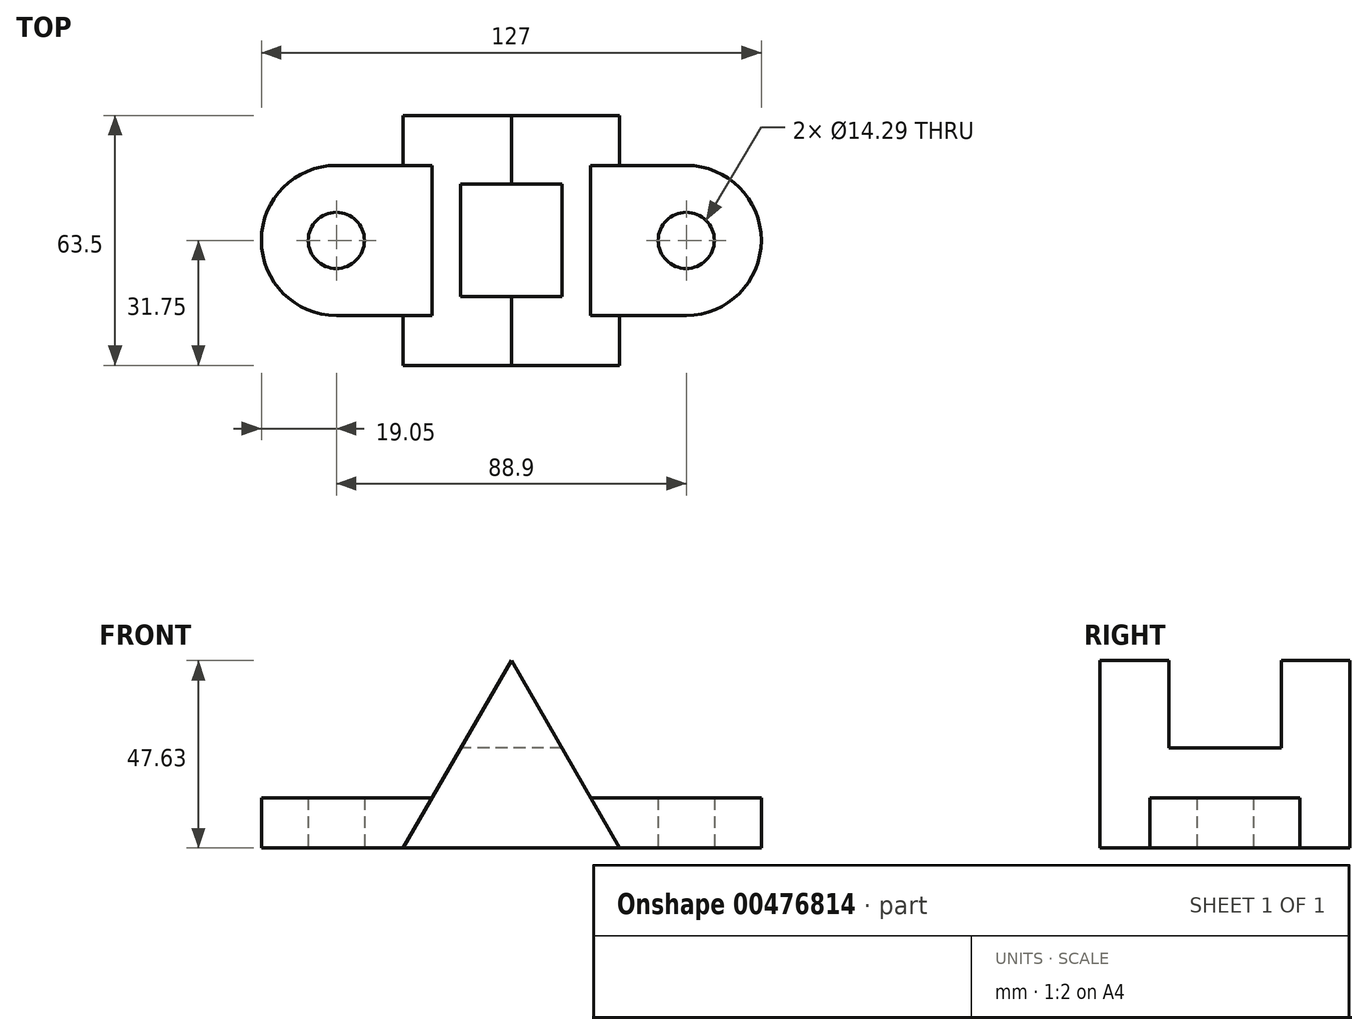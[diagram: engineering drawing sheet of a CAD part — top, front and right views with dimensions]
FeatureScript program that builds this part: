
annotation { "Feature Type Name" : "Feature", "Feature Type Description" : "" }
export const myFeature = defineFeature(function(context is Context, id is Id, definition is map)
    precondition{}
    {
        {
            var Q0;
            Q0=qCreatedBy(makeId("Top.planeOp"),FACE);
            var sketch = newSketch(context, id + "F0", { "sketchPlane" : qUnion([Q0])});
            skArc(sketch, "E0", {"start": v(88.9, -19.05) * mm, "mid": v(107.95, 0) * mm, "end": v(88.9, 19.05) * mm});
            skArc(sketch, "E1", {"start": v(0, 19.05) * mm, "mid": v(-19.05, 0) * mm, "end": v(0, -19.05) * mm});
            skLineSegment(sketch, "E2", {"start": v(0, 19.05) * mm, "end": v(88.9, 19.05) * mm});
            skLineSegment(sketch, "E3", {"start": v(0, -19.05) * mm, "end": v(88.9, -19.05) * mm});
            skCircle(sketch, "E4", {"center": v(0, 0) * mm, "radius": 7.14 * mm});
            skCircle(sketch, "E5", {"center": v(88.9, 0) * mm, "radius": 7.14 * mm});
            skSolve(sketch);
        }
        {
            var Q0;
            Q0=qSketchRegion(id+"F0",true);
            extrude(context, id + "F1", {"entities" : qUnion([Q0]), "depth" : 12.7 * mm});
        }
        {
            var Q0;
            Q0=qCreatedBy(makeId("Front.planeOp"),FACE);
            var sketch = newSketch(context, id + "F2", { "sketchPlane" : qUnion([Q0])});
            skLineSegment(sketch, "E6", {"start": v(16.95, 0) * mm, "end": v(71.95, 0) * mm});
            skLineSegment(sketch, "E7", {"start": v(0, 0) * mm, "end": v(44.45, 0) * mm});
            skLineSegment(sketch, "E8", {"start": v(44.45, 0) * mm, "end": v(44.45, 47.63) * mm});
            skLineSegment(sketch, "E9", {"start": v(44.45, 47.63) * mm, "end": v(16.95, 0) * mm});
            skLineSegment(sketch, "E10", {"start": v(44.45, 47.62) * mm, "end": v(71.95, 0) * mm});
            skSolve(sketch);
        }
        {
            var Q0;
            Q0=qSketchRegion(id+"F2",true);
            extrude(context, id + "F3", {"entities" : qUnion([Q0]), "operationType" : NewBodyOperationType.ADD, "endBound" : BoundingType.SYMMETRIC, "depth" : 63.5 * mm});
        }
        {
            var Q0;
            Q0=qCreatedBy(makeId("Right.planeOp"),FACE);
            var sketch = newSketch(context, id + "F4", { "sketchPlane" : qUnion([Q0])});
            skLineSegment(sketch, "E11", {"start": v(0, 25.4) * mm, "end": v(-14.29, 25.4) * mm});
            skLineSegment(sketch, "E12", {"start": v(-14.29, 25.4) * mm, "end": v(14.29, 25.4) * mm});
            skLineSegment(sketch, "E13", {"start": v(14.29, 25.4) * mm, "end": v(14.29, 47.63) * mm});
            skLineSegment(sketch, "E14", {"start": v(14.29, 47.63) * mm, "end": v(-14.29, 47.63) * mm});
            skLineSegment(sketch, "E15", {"start": v(-14.29, 47.63) * mm, "end": v(-14.29, 25.4) * mm});
            skSolve(sketch);
        }
        {
            var Q0;
            Q0=qSketchRegion(id+"F4",true);
            extrude(context, id + "F5", {"entities" : qUnion([Q0]), "operationType" : NewBodyOperationType.REMOVE, "endBound" : BoundingType.THROUGH_ALL, "depth" : 25.4 * mm});
        }
    });
